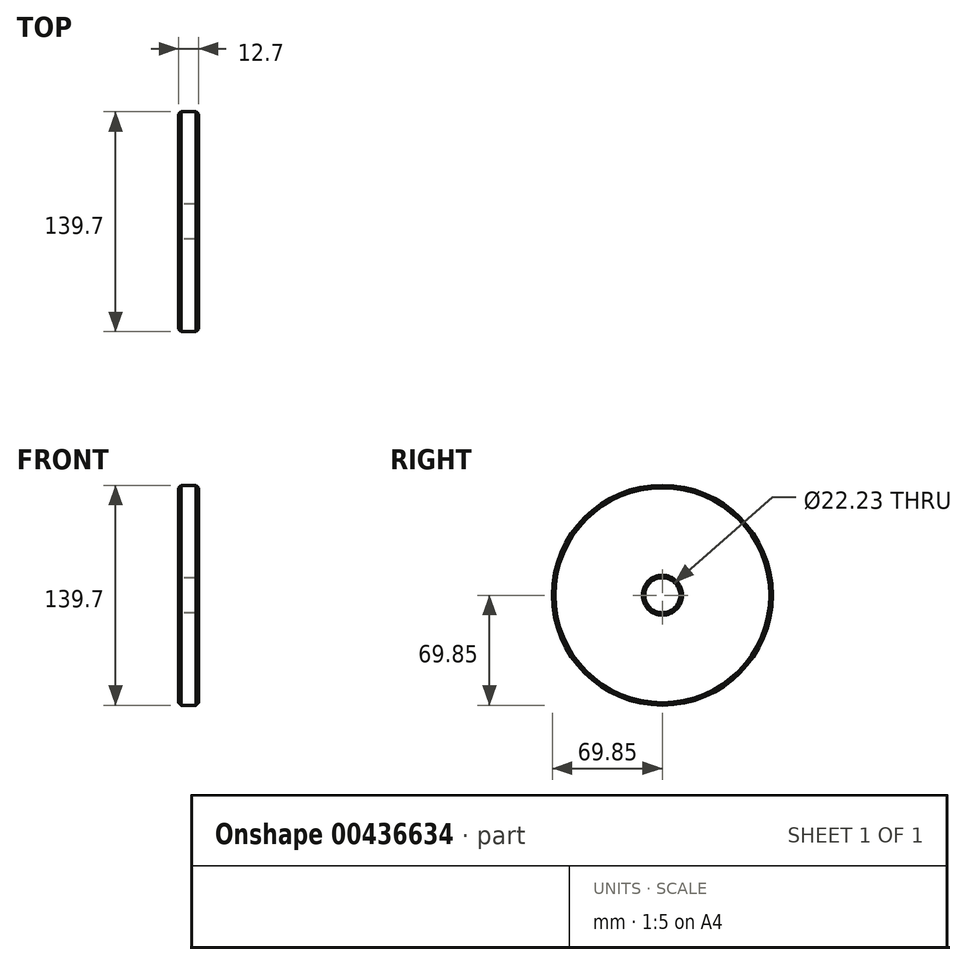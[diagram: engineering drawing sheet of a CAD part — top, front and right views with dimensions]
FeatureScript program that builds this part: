
annotation { "Feature Type Name" : "Feature", "Feature Type Description" : "" }
export const myFeature = defineFeature(function(context is Context, id is Id, definition is map)
    precondition{}
    {
        {
            var Q0;
            Q0=qCreatedBy(makeId("Right.planeOp"),FACE);
            var sketch = newSketch(context, id + "F0", { "sketchPlane" : qUnion([Q0])});
            skCircle(sketch, "E0", {"center": v(0, 0) * mm, "radius": 69.85 * mm});
            skCircle(sketch, "E1", {"center": v(0, 0) * mm, "radius": 11.11 * mm});
            skSolve(sketch);
        }
        {
            var Q0;
            Q0=makeQuery(id+"F0.imprint","IMPRINT",FACE,{"disambiguationData":[TD([[makeQuery(id+"F0.imprint","IMPRINT",EDGE,{"derivedFrom":sQuery(id+"F0.wireOp",EDGE,"E0")}),1.0]])]});
            extrude(context, id + "F1", {"entities" : qUnion([Q0]), "depth" : 12.7 * mm, "offsetDistance" : 25.4 * mm});
        }
        {
            var Q0;
            Q0=makeQuery(id+"F1.opExtrude","CAP_EDGE",EDGE,{"disambiguationData":[OSD([sQuery(id+"F0.wireOp",EDGE,"E1")])],"isStart":true});
            var Q1;
            Q1=makeQuery(id+"F1.opExtrude","CAP_EDGE",EDGE,{"disambiguationData":[OSD([sQuery(id+"F0.wireOp",EDGE,"E1")])],"isStart":false});
            chamfer(context, id + "F2", {"entities" : qUnion([Q0, Q1]), "width" : 1.59 * mm, "tangentPropagation" : true});
        }
        {
            var Q0;
            Q0=makeQuery(id+"F1.opExtrude","CAP_EDGE",EDGE,{"disambiguationData":[OSD([sQuery(id+"F0.wireOp",EDGE,"E0")])],"isStart":true});
            var Q1;
            Q1=makeQuery(id+"F1.opExtrude","CAP_EDGE",EDGE,{"disambiguationData":[OSD([sQuery(id+"F0.wireOp",EDGE,"E0")])],"isStart":false});
            chamfer(context, id + "F3", {"entities" : qUnion([Q0, Q1]), "width" : 1.59 * mm, "tangentPropagation" : true});
        }
    });
